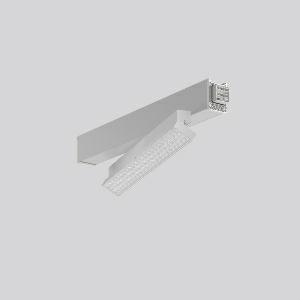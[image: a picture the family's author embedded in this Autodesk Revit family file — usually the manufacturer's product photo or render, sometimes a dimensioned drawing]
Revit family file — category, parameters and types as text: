
# Revit family: linedo_strahlermodule_-_tx-move_950690_840_476_300_620d
name_source: partatom
category: Lighting Fixtures
units: mm (PartAtom-declared; Revit-internal decimal feet)

## family parameters
Cut with Voids When Loaded = No
Host = Face
Light Source = No
Part Type = Normal
Room Calculation Point = No
Round Connector Dimension = Use Diameter
Shared = No

## types (1)
- MultiLumen 1 (1 x LED Modul 840, 2900 lm, 4000)
    Apparent Load = 19 VA
    CIE Flux Codes = 77 96 99 100 100
    Color Rendering = 80
    Color Temperature = 4000
    Default Elevation = 1800 mm
    Description = LINEDO, 19. 40 W, 2900. 5550 lm, 840, silver, DALI
Continuous line luminaire, L 598 B 58 H 131
    Height = 131 mm
    Lamp = 1 x LED Modul 840
    Lamp Light Flux = 2900 lm
    Lamp count = 1
    Length = 598 mm
    Lifetime = 50000 h
    Luminous efficacy = 153 lm/W
    Manufacturer = RZB
    ModVariant = No
    Model = 950690.840.476.300
    Mounting Place = Ceiling
    Mounting Type = Surface mounted
    Number of Poles = 1
    OnlyDefault = Yes
    Power Factor = 1
    Product Name = LINEDO Strahlermodule - TX-MOVE
    Product group = Surface mounted continuous line luminaire system
    ProductGroupID = 310
    Protection Class = Protection class I
    Protection Degree = Degree of protection
    RLX_Detail_Level = 1
    RLX_Emergency_Light_Flux = 0 lm
    RLX_Emergency_Type = 0
    RLX_Emergency_Type_DB = No
    RlxData = <blob elided: 24017 chars, md5=698e42d4>
    Socket = socket
    Standby Power = 0 W
    System Light Flux = 2900 lm
    System Power = 19 W
    Type Comments = MultiLumen 1
    Type Image = 950690.840.476.300.jpg
    URL = http://relux.com
    VarID = multilumen_1
    Voltage = 0 V
    Weight = 0.00 kg
    Width = 58 mm

## geometry (parser evidence)
native form markers: Blend x4, Sweep x15
no freeform markers — native parametric forms only
